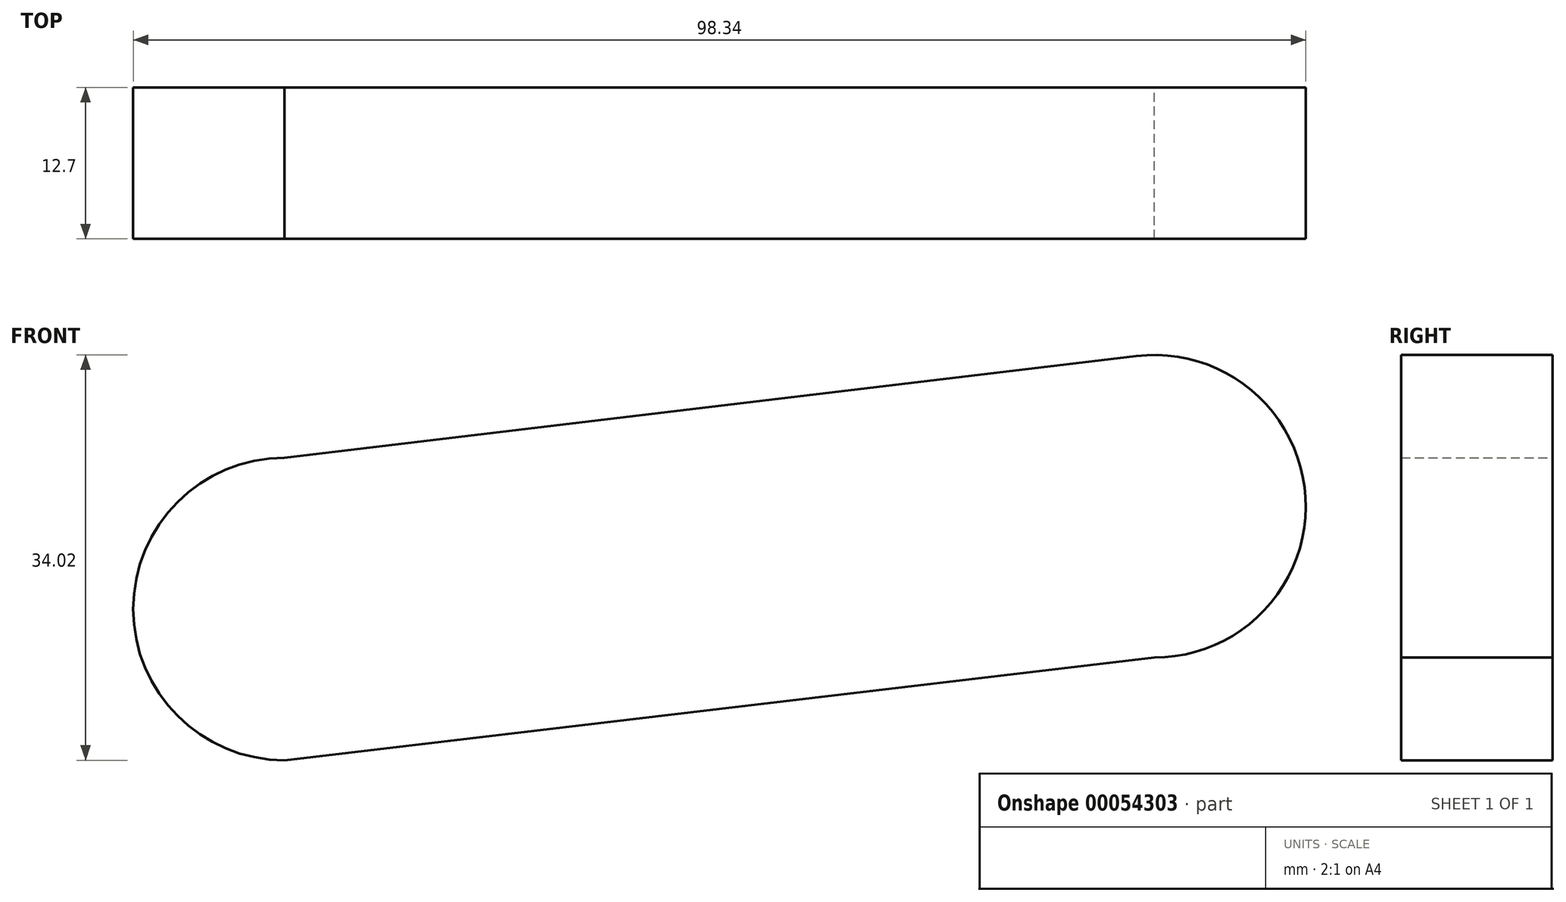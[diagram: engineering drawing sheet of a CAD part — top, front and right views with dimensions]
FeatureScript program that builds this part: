
annotation { "Feature Type Name" : "Feature", "Feature Type Description" : "" }
export const myFeature = defineFeature(function(context is Context, id is Id, definition is map)
    precondition{}
    {
        {
            var Q0;
            Q0=qCreatedBy(makeId("Front.planeOp"),FACE);
            var sketch = newSketch(context, id + "F0", { "sketchPlane" : qUnion([Q0])});
            skCircle(sketch, "E0", {"center": v(-45.4, 45.14) * mm, "radius": 12.7 * mm});
            skCircle(sketch, "E1", {"center": v(27.54, 53.76) * mm, "radius": 12.7 * mm});
            skLineSegment(sketch, "E2", {"start": v(-45.4, 57.84) * mm, "end": v(26.03, 66.37) * mm});
            skLineSegment(sketch, "E3", {"start": v(-45.4, 32.44) * mm, "end": v(27.54, 41.06) * mm});
            skSolve(sketch);
        }
        {
            var Q0;
            {var subQ0=sQuery(id+"F0.wireOp",EDGE,"E2");Q0=makeQuery(id+"F0.imprint","IMPRINT",FACE,{"disambiguationData":[TD([[makeQuery(id+"F0.imprint","IMPRINT",EDGE,{"derivedFrom":subQ0}),-1.0]])]});}
            var Q1;
            {var subQ0=sQuery(id+"F0.wireOp",EDGE,"E0");var subQ1=makeQuery(id+"F0.imprint","INTERSECT",VERTEX,{"derivedFrom":[subQ0,sQuery(id+"F0.wireOp",EDGE,"E2")]});Q1=makeQuery(id+"F0.imprint","IMPRINT",FACE,{"disambiguationData":[TD([[makeQuery(id+"F0.imprint","IMPRINT",EDGE,{"disambiguationData":[TD([[subQ1,-1.0]])],"derivedFrom":subQ0}),1.0]])]});}
            var Q2;
            {var subQ0=sQuery(id+"F0.wireOp",EDGE,"E1");var subQ1=makeQuery(id+"F0.imprint","INTERSECT",VERTEX,{"derivedFrom":[subQ0,sQuery(id+"F0.wireOp",EDGE,"E2")]});Q2=makeQuery(id+"F0.imprint","IMPRINT",FACE,{"disambiguationData":[TD([[makeQuery(id+"F0.imprint","IMPRINT",EDGE,{"disambiguationData":[TD([[subQ1,-1.0]])],"derivedFrom":subQ0}),1.0]])]});}
            extrude(context, id + "F1", {"entities" : qUnion([Q0, Q1, Q2]), "depth" : 12.7 * mm});
        }
    });
